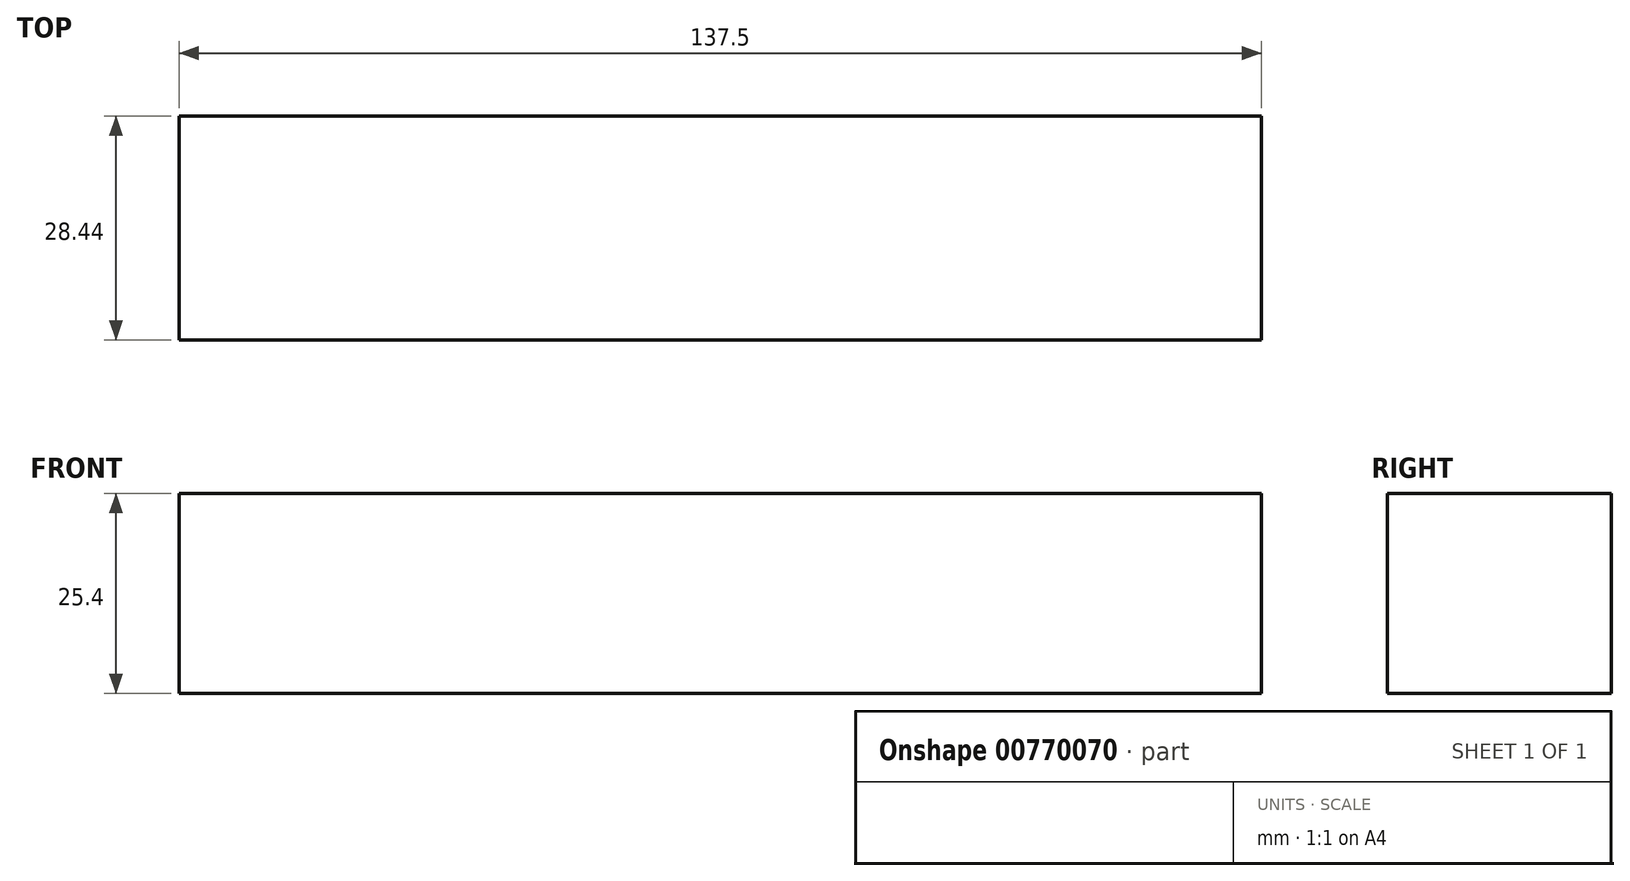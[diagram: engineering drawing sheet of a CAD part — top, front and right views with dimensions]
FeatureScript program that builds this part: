
annotation { "Feature Type Name" : "Feature", "Feature Type Description" : "" }
export const myFeature = defineFeature(function(context is Context, id is Id, definition is map)
    precondition{}
    {
        {
            var Q0;
            Q0=qCreatedBy(makeId("Top.planeOp"),FACE);
            var sketch = newSketch(context, id + "F0", { "sketchPlane" : qUnion([Q0])});
            skLineSegment(sketch, "E0.bottom", {"start": v(64.53, -62.25) * mm, "end": v(-72.97, -62.25) * mm});
            skLineSegment(sketch, "E0.top", {"start": v(64.53, -33.81) * mm, "end": v(-72.97, -33.81) * mm});
            skLineSegment(sketch, "E0.left", {"start": v(64.53, -62.25) * mm, "end": v(64.53, -33.81) * mm});
            skLineSegment(sketch, "E0.right", {"start": v(-72.97, -62.25) * mm, "end": v(-72.97, -33.81) * mm});
            skSolve(sketch);
        }
        {
            var Q0;
            Q0 = qSketchRegion(id + "F0", true);
            extrude(context, id + "F1", {"entities" : qUnion([Q0]), "depth" : 25.4 * mm, "offsetDistance" : 25.4 * mm});
        }
    });
